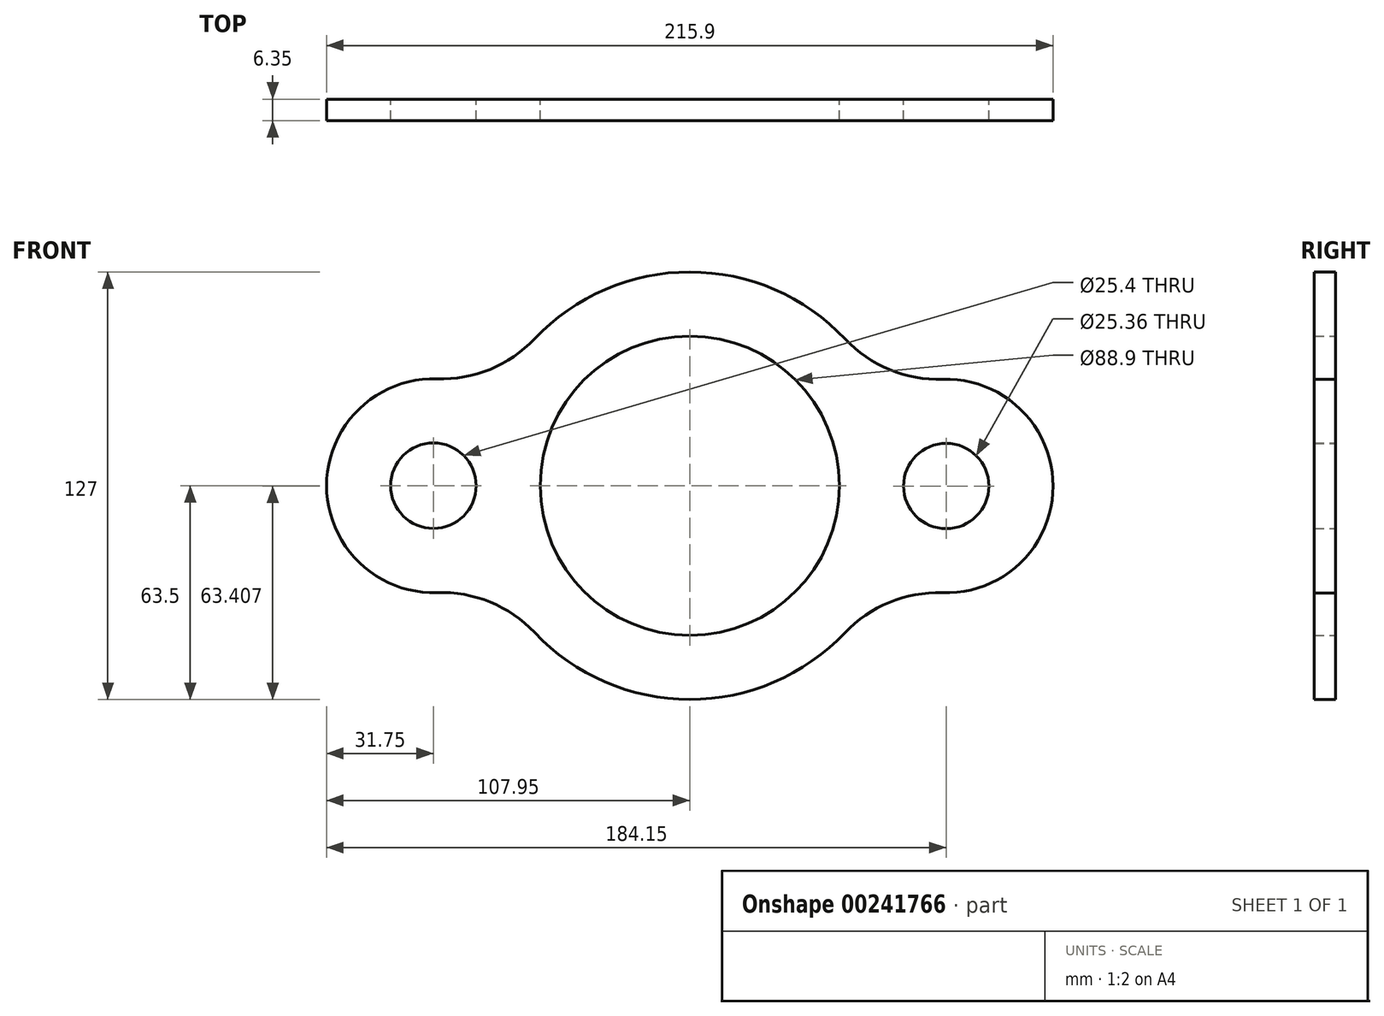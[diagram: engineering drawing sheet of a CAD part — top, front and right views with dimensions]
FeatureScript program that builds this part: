
annotation { "Feature Type Name" : "Feature", "Feature Type Description" : "" }
export const myFeature = defineFeature(function(context is Context, id is Id, definition is map)
    precondition{}
    {
        {
            var Q0;
            Q0=qCreatedBy(makeId("Front.planeOp"),FACE);
            var sketch = newSketch(context, id + "F0", { "sketchPlane" : qUnion([Q0])});
            skCircle(sketch, "E0", {"center": v(-76.2, 0) * mm, "radius": 12.7 * mm});
            skCircle(sketch, "E1", {"center": v(76.2, -0.1) * mm, "radius": 12.68 * mm});
            skArc(sketch, "E2", {"start": v(-75.12, 31.73) * mm, "mid": v(-107.95, 0) * mm, "end": v(-75.12, -31.73) * mm});
            skArc(sketch, "E3", {"start": v(75.08, -31.82) * mm, "mid": v(107.95, -0.13) * mm, "end": v(75.16, 31.64) * mm});
            skArc(sketch, "E4", {"start": v(-46.14, -43.63) * mm, "mid": v(-0.04, -63.5) * mm, "end": v(46.08, -43.69) * mm});
            skCircle(sketch, "E5", {"center": v(0, 0) * mm, "radius": 44.45 * mm});
            skArc(sketch, "E6.filletArc", {"start": v(-75.12, 31.73) * mm, "mid": v(-59.35, 34.56) * mm, "end": v(-46.14, 43.63) * mm});
            skArc(sketch, "E7.filletArc", {"start": v(-46.14, -43.63) * mm, "mid": v(-59.35, -34.56) * mm, "end": v(-75.12, -31.73) * mm});
            skArc(sketch, "E8.trimOffspring", {"start": v(46.2, 43.57) * mm, "mid": v(0.04, 63.5) * mm, "end": v(-46.14, 43.63) * mm});
            skPoint(sketch, "E9.visualSharp", {"position": v(57.98, 25.9) * mm});
            skArc(sketch, "E9.filletArc", {"start": v(46.2, 43.57) * mm, "mid": v(59.39, 34.5) * mm, "end": v(75.16, 31.64) * mm});
            skPoint(sketch, "E10.visualSharp", {"position": v(57.91, -26.05) * mm});
            skArc(sketch, "E10.filletArc", {"start": v(75.08, -31.82) * mm, "mid": v(59.3, -34.64) * mm, "end": v(46.08, -43.69) * mm});
            skSolve(sketch);
        }
        {
            var Q0;
            Q0 = qSketchRegion(id + "F0", true);
            extrude(context, id + "F1", {"entities" : qUnion([Q0]), "depth" : 6.35 * mm});
        }
    });
